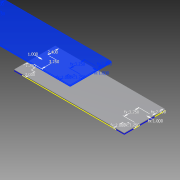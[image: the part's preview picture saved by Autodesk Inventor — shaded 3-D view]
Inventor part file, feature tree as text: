
AUTODESK INVENTOR PART (.ipt)
format: ipt  version: 2012 (Build 160160000, 160)  size: 89,600 bytes
history: native  units: in
note: dims shown in document units (in); Inventor stores cm internally (conversion verified against a paired STEP export)
features: sketch x2, extrude x1
ambient origin geometry x8: Origin, YZ Plane, XZ Plane, XY Plane, X Axis, Y Axis, Z Axis, Center Point
bodies: Solid1 (feature_tree)
feature tree (3):
  extrude  "Extrusion1"  Depth=0.2in
  sketch  "Sketch2"  dims[d2=9.0in d3=0.0in d4=1.75in d5=2.0in d6=1.75in d7=2.0in d8=2.4in d9=2.4in d10=1.0in d11=1.0in d12=3.25in d13=3.25in]
  sketch  "Sketch1"  dims[d0=24.0in d1=0.2in]
